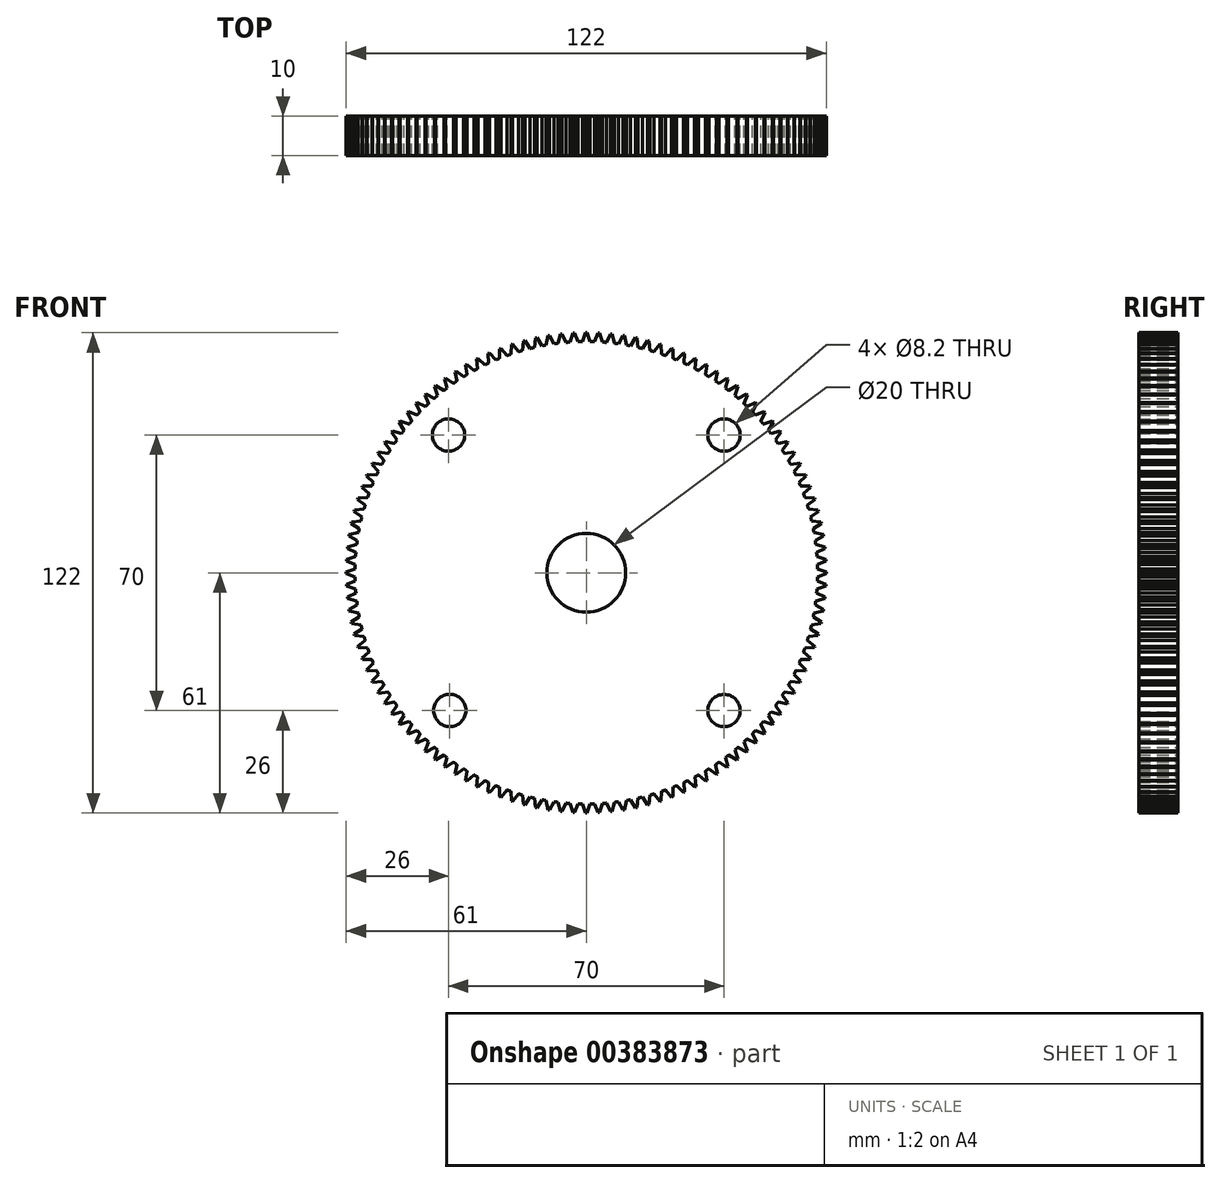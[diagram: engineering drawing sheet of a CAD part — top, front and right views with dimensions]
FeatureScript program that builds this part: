
annotation { "Feature Type Name" : "Feature", "Feature Type Description" : "" }
export const myFeature = defineFeature(function(context is Context, id is Id, definition is map)
    precondition{}
    {
        {
            var Q0;
            Q0=qCreatedBy(makeId("Front.planeOp"),FACE);
            var sketch = newSketch(context, id + "F0", { "sketchPlane" : qUnion([Q0])});
            skCircle(sketch, "E0", {"center": v(0, 0) * mm, "radius": 58.75 * mm});
            skCircle(sketch, "E1", {"center": v(0, 0) * mm, "radius": 61 * mm, "construction": true});
            skLineSegment(sketch, "E2", {"start": v(-1, 58.74) * mm, "end": v(-0.19, 61) * mm});
            skLineSegment(sketch, "E3", {"start": v(-0.19, 61) * mm, "end": v(0, 61) * mm});
            skLineSegment(sketch, "E4", {"start": v(-1, 58.74) * mm, "end": v(-1, 61.95) * mm, "construction": true});
            skLineSegment(sketch, "E5.MirrorCS", {"start": v(0.19, 61) * mm, "end": v(0, 61) * mm});
            skLineSegment(sketch, "E6.MirrorCS", {"start": v(1, 58.74) * mm, "end": v(0.19, 61) * mm});
            skLineSegment(sketch, "E7.1.0", {"start": v(-4.08, 58.6) * mm, "end": v(-3.38, 60.9) * mm});
            skLineSegment(sketch, "E7.1.1", {"start": v(-3.38, 60.9) * mm, "end": v(-3.2, 60.92) * mm});
            skLineSegment(sketch, "E7.1.2", {"start": v(-3, 60.93) * mm, "end": v(-3.2, 60.92) * mm});
            skLineSegment(sketch, "E7.1.3", {"start": v(-2.07, 58.71) * mm, "end": v(-3, 60.93) * mm});
            skLineSegment(sketch, "E7.2.0", {"start": v(-7.14, 58.31) * mm, "end": v(-6.56, 60.65) * mm});
            skLineSegment(sketch, "E7.2.1", {"start": v(-6.56, 60.65) * mm, "end": v(-6.38, 60.67) * mm});
            skLineSegment(sketch, "E7.2.2", {"start": v(-6.19, 60.69) * mm, "end": v(-6.38, 60.67) * mm});
            skLineSegment(sketch, "E7.2.3", {"start": v(-5.14, 58.53) * mm, "end": v(-6.19, 60.69) * mm});
            skLineSegment(sketch, "E7.3.0", {"start": v(-10.19, 57.86) * mm, "end": v(-9.73, 60.22) * mm});
            skLineSegment(sketch, "E7.3.1", {"start": v(-9.73, 60.22) * mm, "end": v(-9.54, 60.25) * mm});
            skLineSegment(sketch, "E7.3.2", {"start": v(-9.36, 60.28) * mm, "end": v(-9.54, 60.25) * mm});
            skLineSegment(sketch, "E7.3.3", {"start": v(-8.2, 58.18) * mm, "end": v(-9.36, 60.28) * mm});
            skLineSegment(sketch, "E7.4.0", {"start": v(-13.2, 57.25) * mm, "end": v(-12.87, 59.63) * mm});
            skLineSegment(sketch, "E7.4.1", {"start": v(-12.87, 59.63) * mm, "end": v(-12.68, 59.67) * mm});
            skLineSegment(sketch, "E7.4.2", {"start": v(-12.5, 59.7) * mm, "end": v(-12.68, 59.67) * mm});
            skLineSegment(sketch, "E7.4.3", {"start": v(-11.23, 57.67) * mm, "end": v(-12.5, 59.7) * mm});
            skLineSegment(sketch, "E7.5.0", {"start": v(-16.18, 56.48) * mm, "end": v(-15.97, 58.87) * mm});
            skLineSegment(sketch, "E7.5.1", {"start": v(-15.97, 58.87) * mm, "end": v(-15.79, 58.92) * mm});
            skLineSegment(sketch, "E7.5.2", {"start": v(-15.6, 58.97) * mm, "end": v(-15.79, 58.92) * mm});
            skLineSegment(sketch, "E7.5.3", {"start": v(-14.23, 57) * mm, "end": v(-15.6, 58.97) * mm});
            skLineSegment(sketch, "E7.6.0", {"start": v(-19.11, 55.55) * mm, "end": v(-19.03, 57.96) * mm});
            skLineSegment(sketch, "E7.6.1", {"start": v(-19.03, 57.96) * mm, "end": v(-18.85, 58.01) * mm});
            skLineSegment(sketch, "E7.6.2", {"start": v(-18.67, 58.07) * mm, "end": v(-18.85, 58.01) * mm});
            skLineSegment(sketch, "E7.6.3", {"start": v(-17.2, 56.18) * mm, "end": v(-18.67, 58.07) * mm});
            skLineSegment(sketch, "E7.7.0", {"start": v(-22, 54.48) * mm, "end": v(-22.04, 56.88) * mm});
            skLineSegment(sketch, "E7.7.1", {"start": v(-22.04, 56.88) * mm, "end": v(-21.86, 56.95) * mm});
            skLineSegment(sketch, "E7.7.2", {"start": v(-21.69, 57.02) * mm, "end": v(-21.86, 56.95) * mm});
            skLineSegment(sketch, "E7.7.3", {"start": v(-20.1, 55.2) * mm, "end": v(-21.69, 57.02) * mm});
            skLineSegment(sketch, "E7.8.0", {"start": v(-24.81, 53.25) * mm, "end": v(-24.98, 55.65) * mm});
            skLineSegment(sketch, "E7.8.1", {"start": v(-24.98, 55.65) * mm, "end": v(-24.81, 55.73) * mm});
            skLineSegment(sketch, "E7.8.2", {"start": v(-24.64, 55.8) * mm, "end": v(-24.81, 55.73) * mm});
            skLineSegment(sketch, "E7.8.3", {"start": v(-22.97, 54.07) * mm, "end": v(-24.64, 55.8) * mm});
            skLineSegment(sketch, "E7.9.0", {"start": v(-27.57, 51.88) * mm, "end": v(-27.86, 54.27) * mm});
            skLineSegment(sketch, "E7.9.1", {"start": v(-27.86, 54.27) * mm, "end": v(-27.7, 54.35) * mm});
            skLineSegment(sketch, "E7.9.2", {"start": v(-27.53, 54.44) * mm, "end": v(-27.7, 54.35) * mm});
            skLineSegment(sketch, "E7.9.3", {"start": v(-25.77, 52.8) * mm, "end": v(-27.53, 54.44) * mm});
            skLineSegment(sketch, "E7.10.0", {"start": v(-30.24, 50.37) * mm, "end": v(-30.66, 52.73) * mm});
            skLineSegment(sketch, "E7.10.1", {"start": v(-30.66, 52.73) * mm, "end": v(-30.5, 52.83) * mm});
            skLineSegment(sketch, "E7.10.2", {"start": v(-30.34, 52.92) * mm, "end": v(-30.5, 52.83) * mm});
            skLineSegment(sketch, "E7.10.3", {"start": v(-28.5, 51.38) * mm, "end": v(-30.34, 52.92) * mm});
            skLineSegment(sketch, "E7.11.0", {"start": v(-32.84, 48.71) * mm, "end": v(-33.38, 51.06) * mm});
            skLineSegment(sketch, "E7.11.1", {"start": v(-33.38, 51.06) * mm, "end": v(-33.22, 51.16) * mm});
            skLineSegment(sketch, "E7.11.2", {"start": v(-33.07, 51.26) * mm, "end": v(-33.22, 51.16) * mm});
            skLineSegment(sketch, "E7.11.3", {"start": v(-31.15, 49.81) * mm, "end": v(-33.07, 51.26) * mm});
            skLineSegment(sketch, "E8.1.12.0", {"start": v(-35.34, 46.93) * mm, "end": v(-36, 49.24) * mm});
            skLineSegment(sketch, "E8.3.12.0", {"start": v(-36, 49.24) * mm, "end": v(-35.85, 49.35) * mm});
            skLineSegment(sketch, "E8.6.12.0", {"start": v(-35.7, 49.46) * mm, "end": v(-35.85, 49.35) * mm});
            skLineSegment(sketch, "E8.9.12.0", {"start": v(-33.71, 48.12) * mm, "end": v(-35.7, 49.46) * mm});
            skLineSegment(sketch, "E8.1.13.0", {"start": v(-37.75, 45.02) * mm, "end": v(-38.53, 47.29) * mm});
            skLineSegment(sketch, "E8.3.13.0", {"start": v(-38.53, 47.29) * mm, "end": v(-38.39, 47.4) * mm});
            skLineSegment(sketch, "E8.6.13.0", {"start": v(-38.24, 47.52) * mm, "end": v(-38.39, 47.4) * mm});
            skLineSegment(sketch, "E8.9.13.0", {"start": v(-36.18, 46.29) * mm, "end": v(-38.24, 47.52) * mm});
            skLineSegment(sketch, "E8.1.14.0", {"start": v(-40.06, 42.98) * mm, "end": v(-40.96, 45.2) * mm});
            skLineSegment(sketch, "E8.3.14.0", {"start": v(-40.96, 45.2) * mm, "end": v(-40.82, 45.33) * mm});
            skLineSegment(sketch, "E8.6.14.0", {"start": v(-40.68, 45.46) * mm, "end": v(-40.82, 45.33) * mm});
            skLineSegment(sketch, "E8.9.14.0", {"start": v(-38.56, 44.33) * mm, "end": v(-40.68, 45.46) * mm});
            skLineSegment(sketch, "E8.1.15.0", {"start": v(-42.25, 40.82) * mm, "end": v(-43.27, 43) * mm});
            skLineSegment(sketch, "E8.3.15.0", {"start": v(-43.27, 43) * mm, "end": v(-43.13, 43.13) * mm});
            skLineSegment(sketch, "E8.6.15.0", {"start": v(-43, 43.27) * mm, "end": v(-43.13, 43.13) * mm});
            skLineSegment(sketch, "E8.9.15.0", {"start": v(-40.82, 42.25) * mm, "end": v(-43, 43.27) * mm});
            skLineSegment(sketch, "E8.1.16.0", {"start": v(-44.33, 38.56) * mm, "end": v(-45.46, 40.68) * mm});
            skLineSegment(sketch, "E8.3.16.0", {"start": v(-45.46, 40.68) * mm, "end": v(-45.33, 40.82) * mm});
            skLineSegment(sketch, "E8.6.16.0", {"start": v(-45.2, 40.96) * mm, "end": v(-45.33, 40.82) * mm});
            skLineSegment(sketch, "E8.9.16.0", {"start": v(-42.98, 40.06) * mm, "end": v(-45.2, 40.96) * mm});
            skLineSegment(sketch, "E8.1.17.0", {"start": v(-46.29, 36.18) * mm, "end": v(-47.52, 38.24) * mm});
            skLineSegment(sketch, "E8.3.17.0", {"start": v(-47.52, 38.24) * mm, "end": v(-47.4, 38.39) * mm});
            skLineSegment(sketch, "E8.6.17.0", {"start": v(-47.29, 38.53) * mm, "end": v(-47.4, 38.39) * mm});
            skLineSegment(sketch, "E8.9.17.0", {"start": v(-45.02, 37.75) * mm, "end": v(-47.29, 38.53) * mm});
            skLineSegment(sketch, "E8.1.18.0", {"start": v(-48.12, 33.71) * mm, "end": v(-49.46, 35.7) * mm});
            skLineSegment(sketch, "E8.3.18.0", {"start": v(-49.46, 35.7) * mm, "end": v(-49.35, 35.85) * mm});
            skLineSegment(sketch, "E8.6.18.0", {"start": v(-49.24, 36) * mm, "end": v(-49.35, 35.85) * mm});
            skLineSegment(sketch, "E8.9.18.0", {"start": v(-46.93, 35.34) * mm, "end": v(-49.24, 36) * mm});
            skLineSegment(sketch, "E8.1.19.0", {"start": v(-49.81, 31.15) * mm, "end": v(-51.26, 33.07) * mm});
            skLineSegment(sketch, "E8.3.19.0", {"start": v(-51.26, 33.07) * mm, "end": v(-51.16, 33.22) * mm});
            skLineSegment(sketch, "E8.6.19.0", {"start": v(-51.06, 33.38) * mm, "end": v(-51.16, 33.22) * mm});
            skLineSegment(sketch, "E8.9.19.0", {"start": v(-48.71, 32.84) * mm, "end": v(-51.06, 33.38) * mm});
            skLineSegment(sketch, "E8.1.20.0", {"start": v(-51.38, 28.5) * mm, "end": v(-52.92, 30.34) * mm});
            skLineSegment(sketch, "E8.3.20.0", {"start": v(-52.92, 30.34) * mm, "end": v(-52.83, 30.5) * mm});
            skLineSegment(sketch, "E8.6.20.0", {"start": v(-52.73, 30.66) * mm, "end": v(-52.83, 30.5) * mm});
            skLineSegment(sketch, "E8.9.20.0", {"start": v(-50.37, 30.24) * mm, "end": v(-52.73, 30.66) * mm});
            skLineSegment(sketch, "E8.1.21.0", {"start": v(-52.8, 25.77) * mm, "end": v(-54.44, 27.53) * mm});
            skLineSegment(sketch, "E8.3.21.0", {"start": v(-54.44, 27.53) * mm, "end": v(-54.35, 27.7) * mm});
            skLineSegment(sketch, "E8.6.21.0", {"start": v(-54.27, 27.86) * mm, "end": v(-54.35, 27.7) * mm});
            skLineSegment(sketch, "E8.9.21.0", {"start": v(-51.88, 27.57) * mm, "end": v(-54.27, 27.86) * mm});
            skLineSegment(sketch, "E8.1.22.0", {"start": v(-54.07, 22.97) * mm, "end": v(-55.8, 24.64) * mm});
            skLineSegment(sketch, "E8.3.22.0", {"start": v(-55.8, 24.64) * mm, "end": v(-55.73, 24.81) * mm});
            skLineSegment(sketch, "E8.6.22.0", {"start": v(-55.65, 24.98) * mm, "end": v(-55.73, 24.81) * mm});
            skLineSegment(sketch, "E8.9.22.0", {"start": v(-53.25, 24.81) * mm, "end": v(-55.65, 24.98) * mm});
            skLineSegment(sketch, "E8.1.23.0", {"start": v(-55.2, 20.1) * mm, "end": v(-57.02, 21.69) * mm});
            skLineSegment(sketch, "E8.3.23.0", {"start": v(-57.02, 21.69) * mm, "end": v(-56.95, 21.86) * mm});
            skLineSegment(sketch, "E8.6.23.0", {"start": v(-56.88, 22.04) * mm, "end": v(-56.95, 21.86) * mm});
            skLineSegment(sketch, "E8.9.23.0", {"start": v(-54.48, 22) * mm, "end": v(-56.88, 22.04) * mm});
            skLineSegment(sketch, "E8.1.24.0", {"start": v(-56.18, 17.2) * mm, "end": v(-58.07, 18.67) * mm});
            skLineSegment(sketch, "E8.3.24.0", {"start": v(-58.07, 18.67) * mm, "end": v(-58.01, 18.85) * mm});
            skLineSegment(sketch, "E8.6.24.0", {"start": v(-57.96, 19.03) * mm, "end": v(-58.01, 18.85) * mm});
            skLineSegment(sketch, "E8.9.24.0", {"start": v(-55.55, 19.11) * mm, "end": v(-57.96, 19.03) * mm});
            skLineSegment(sketch, "E8.1.25.0", {"start": v(-57, 14.23) * mm, "end": v(-58.97, 15.6) * mm});
            skLineSegment(sketch, "E8.3.25.0", {"start": v(-58.97, 15.6) * mm, "end": v(-58.92, 15.79) * mm});
            skLineSegment(sketch, "E8.6.25.0", {"start": v(-58.87, 15.97) * mm, "end": v(-58.92, 15.79) * mm});
            skLineSegment(sketch, "E8.9.25.0", {"start": v(-56.48, 16.18) * mm, "end": v(-58.87, 15.97) * mm});
            skLineSegment(sketch, "E8.1.26.0", {"start": v(-57.67, 11.23) * mm, "end": v(-59.7, 12.5) * mm});
            skLineSegment(sketch, "E8.3.26.0", {"start": v(-59.7, 12.5) * mm, "end": v(-59.67, 12.68) * mm});
            skLineSegment(sketch, "E8.6.26.0", {"start": v(-59.63, 12.87) * mm, "end": v(-59.67, 12.68) * mm});
            skLineSegment(sketch, "E8.9.26.0", {"start": v(-57.25, 13.2) * mm, "end": v(-59.63, 12.87) * mm});
            skLineSegment(sketch, "E8.1.27.0", {"start": v(-58.18, 8.2) * mm, "end": v(-60.28, 9.36) * mm});
            skLineSegment(sketch, "E8.3.27.0", {"start": v(-60.28, 9.36) * mm, "end": v(-60.25, 9.54) * mm});
            skLineSegment(sketch, "E8.6.27.0", {"start": v(-60.22, 9.73) * mm, "end": v(-60.25, 9.54) * mm});
            skLineSegment(sketch, "E8.9.27.0", {"start": v(-57.86, 10.19) * mm, "end": v(-60.22, 9.73) * mm});
            skLineSegment(sketch, "E8.1.28.0", {"start": v(-58.53, 5.14) * mm, "end": v(-60.69, 6.19) * mm});
            skLineSegment(sketch, "E8.3.28.0", {"start": v(-60.69, 6.19) * mm, "end": v(-60.67, 6.38) * mm});
            skLineSegment(sketch, "E8.6.28.0", {"start": v(-60.65, 6.56) * mm, "end": v(-60.67, 6.38) * mm});
            skLineSegment(sketch, "E8.9.28.0", {"start": v(-58.31, 7.14) * mm, "end": v(-60.65, 6.56) * mm});
            skLineSegment(sketch, "E8.1.29.0", {"start": v(-58.71, 2.07) * mm, "end": v(-60.93, 3) * mm});
            skLineSegment(sketch, "E8.3.29.0", {"start": v(-60.93, 3) * mm, "end": v(-60.92, 3.2) * mm});
            skLineSegment(sketch, "E8.6.29.0", {"start": v(-60.9, 3.38) * mm, "end": v(-60.92, 3.2) * mm});
            skLineSegment(sketch, "E8.9.29.0", {"start": v(-58.6, 4.08) * mm, "end": v(-60.9, 3.38) * mm});
            skLineSegment(sketch, "E8.1.30.0", {"start": v(-58.74, -1) * mm, "end": v(-61, -0.19) * mm});
            skLineSegment(sketch, "E8.3.30.0", {"start": v(-61, -0.19) * mm, "end": v(-61, 0) * mm});
            skLineSegment(sketch, "E8.6.30.0", {"start": v(-61, 0.19) * mm, "end": v(-61, 0) * mm});
            skLineSegment(sketch, "E8.9.30.0", {"start": v(-58.74, 1) * mm, "end": v(-61, 0.19) * mm});
            skLineSegment(sketch, "E8.1.31.0", {"start": v(-58.6, -4.08) * mm, "end": v(-60.9, -3.38) * mm});
            skLineSegment(sketch, "E8.3.31.0", {"start": v(-60.9, -3.38) * mm, "end": v(-60.92, -3.2) * mm});
            skLineSegment(sketch, "E8.6.31.0", {"start": v(-60.93, -3) * mm, "end": v(-60.92, -3.2) * mm});
            skLineSegment(sketch, "E8.9.31.0", {"start": v(-58.71, -2.07) * mm, "end": v(-60.93, -3) * mm});
            skLineSegment(sketch, "E8.1.32.0", {"start": v(-58.31, -7.14) * mm, "end": v(-60.65, -6.56) * mm});
            skLineSegment(sketch, "E8.3.32.0", {"start": v(-60.65, -6.56) * mm, "end": v(-60.67, -6.38) * mm});
            skLineSegment(sketch, "E8.6.32.0", {"start": v(-60.69, -6.19) * mm, "end": v(-60.67, -6.38) * mm});
            skLineSegment(sketch, "E8.9.32.0", {"start": v(-58.53, -5.14) * mm, "end": v(-60.69, -6.19) * mm});
            skLineSegment(sketch, "E8.1.33.0", {"start": v(-57.86, -10.19) * mm, "end": v(-60.22, -9.73) * mm});
            skLineSegment(sketch, "E8.3.33.0", {"start": v(-60.22, -9.73) * mm, "end": v(-60.25, -9.54) * mm});
            skLineSegment(sketch, "E8.6.33.0", {"start": v(-60.28, -9.36) * mm, "end": v(-60.25, -9.54) * mm});
            skLineSegment(sketch, "E8.9.33.0", {"start": v(-58.18, -8.2) * mm, "end": v(-60.28, -9.36) * mm});
            skLineSegment(sketch, "E8.1.34.0", {"start": v(-57.25, -13.2) * mm, "end": v(-59.63, -12.87) * mm});
            skLineSegment(sketch, "E8.3.34.0", {"start": v(-59.63, -12.87) * mm, "end": v(-59.67, -12.68) * mm});
            skLineSegment(sketch, "E8.6.34.0", {"start": v(-59.7, -12.5) * mm, "end": v(-59.67, -12.68) * mm});
            skLineSegment(sketch, "E8.9.34.0", {"start": v(-57.67, -11.23) * mm, "end": v(-59.7, -12.5) * mm});
            skLineSegment(sketch, "E8.1.35.0", {"start": v(-56.48, -16.18) * mm, "end": v(-58.87, -15.97) * mm});
            skLineSegment(sketch, "E8.3.35.0", {"start": v(-58.87, -15.97) * mm, "end": v(-58.92, -15.79) * mm});
            skLineSegment(sketch, "E8.6.35.0", {"start": v(-58.97, -15.6) * mm, "end": v(-58.92, -15.79) * mm});
            skLineSegment(sketch, "E8.9.35.0", {"start": v(-57, -14.23) * mm, "end": v(-58.97, -15.6) * mm});
            skLineSegment(sketch, "E8.1.36.0", {"start": v(-55.55, -19.11) * mm, "end": v(-57.96, -19.03) * mm});
            skLineSegment(sketch, "E8.3.36.0", {"start": v(-57.96, -19.03) * mm, "end": v(-58.01, -18.85) * mm});
            skLineSegment(sketch, "E8.6.36.0", {"start": v(-58.07, -18.67) * mm, "end": v(-58.01, -18.85) * mm});
            skLineSegment(sketch, "E8.9.36.0", {"start": v(-56.18, -17.2) * mm, "end": v(-58.07, -18.67) * mm});
            skLineSegment(sketch, "E8.1.37.0", {"start": v(-54.48, -22) * mm, "end": v(-56.88, -22.04) * mm});
            skLineSegment(sketch, "E8.3.37.0", {"start": v(-56.88, -22.04) * mm, "end": v(-56.95, -21.86) * mm});
            skLineSegment(sketch, "E8.6.37.0", {"start": v(-57.02, -21.69) * mm, "end": v(-56.95, -21.86) * mm});
            skLineSegment(sketch, "E8.9.37.0", {"start": v(-55.2, -20.1) * mm, "end": v(-57.02, -21.69) * mm});
            skLineSegment(sketch, "E8.1.38.0", {"start": v(-53.25, -24.81) * mm, "end": v(-55.65, -24.98) * mm});
            skLineSegment(sketch, "E8.3.38.0", {"start": v(-55.65, -24.98) * mm, "end": v(-55.73, -24.81) * mm});
            skLineSegment(sketch, "E8.6.38.0", {"start": v(-55.8, -24.64) * mm, "end": v(-55.73, -24.81) * mm});
            skLineSegment(sketch, "E8.9.38.0", {"start": v(-54.07, -22.97) * mm, "end": v(-55.8, -24.64) * mm});
            skLineSegment(sketch, "E8.1.39.0", {"start": v(-51.88, -27.57) * mm, "end": v(-54.27, -27.86) * mm});
            skLineSegment(sketch, "E8.3.39.0", {"start": v(-54.27, -27.86) * mm, "end": v(-54.35, -27.7) * mm});
            skLineSegment(sketch, "E8.6.39.0", {"start": v(-54.44, -27.53) * mm, "end": v(-54.35, -27.7) * mm});
            skLineSegment(sketch, "E8.9.39.0", {"start": v(-52.8, -25.77) * mm, "end": v(-54.44, -27.53) * mm});
            skLineSegment(sketch, "E8.1.40.0", {"start": v(-50.37, -30.24) * mm, "end": v(-52.73, -30.66) * mm});
            skLineSegment(sketch, "E8.3.40.0", {"start": v(-52.73, -30.66) * mm, "end": v(-52.83, -30.5) * mm});
            skLineSegment(sketch, "E8.6.40.0", {"start": v(-52.92, -30.34) * mm, "end": v(-52.83, -30.5) * mm});
            skLineSegment(sketch, "E8.9.40.0", {"start": v(-51.38, -28.5) * mm, "end": v(-52.92, -30.34) * mm});
            skLineSegment(sketch, "E8.1.41.0", {"start": v(-48.71, -32.84) * mm, "end": v(-51.06, -33.38) * mm});
            skLineSegment(sketch, "E8.3.41.0", {"start": v(-51.06, -33.38) * mm, "end": v(-51.16, -33.22) * mm});
            skLineSegment(sketch, "E8.6.41.0", {"start": v(-51.26, -33.07) * mm, "end": v(-51.16, -33.22) * mm});
            skLineSegment(sketch, "E8.9.41.0", {"start": v(-49.81, -31.15) * mm, "end": v(-51.26, -33.07) * mm});
            skLineSegment(sketch, "E8.1.42.0", {"start": v(-46.93, -35.34) * mm, "end": v(-49.24, -36) * mm});
            skLineSegment(sketch, "E8.3.42.0", {"start": v(-49.24, -36) * mm, "end": v(-49.35, -35.85) * mm});
            skLineSegment(sketch, "E8.6.42.0", {"start": v(-49.46, -35.7) * mm, "end": v(-49.35, -35.85) * mm});
            skLineSegment(sketch, "E8.9.42.0", {"start": v(-48.12, -33.71) * mm, "end": v(-49.46, -35.7) * mm});
            skLineSegment(sketch, "E8.1.43.0", {"start": v(-45.02, -37.75) * mm, "end": v(-47.29, -38.53) * mm});
            skLineSegment(sketch, "E8.3.43.0", {"start": v(-47.29, -38.53) * mm, "end": v(-47.4, -38.39) * mm});
            skLineSegment(sketch, "E8.6.43.0", {"start": v(-47.52, -38.24) * mm, "end": v(-47.4, -38.39) * mm});
            skLineSegment(sketch, "E8.9.43.0", {"start": v(-46.29, -36.18) * mm, "end": v(-47.52, -38.24) * mm});
            skLineSegment(sketch, "E8.1.44.0", {"start": v(-42.98, -40.06) * mm, "end": v(-45.2, -40.96) * mm});
            skLineSegment(sketch, "E8.3.44.0", {"start": v(-45.2, -40.96) * mm, "end": v(-45.33, -40.82) * mm});
            skLineSegment(sketch, "E8.6.44.0", {"start": v(-45.46, -40.68) * mm, "end": v(-45.33, -40.82) * mm});
            skLineSegment(sketch, "E8.9.44.0", {"start": v(-44.33, -38.56) * mm, "end": v(-45.46, -40.68) * mm});
            skLineSegment(sketch, "E8.1.45.0", {"start": v(-40.82, -42.25) * mm, "end": v(-43, -43.27) * mm});
            skLineSegment(sketch, "E8.3.45.0", {"start": v(-43, -43.27) * mm, "end": v(-43.13, -43.13) * mm});
            skLineSegment(sketch, "E8.6.45.0", {"start": v(-43.27, -43) * mm, "end": v(-43.13, -43.13) * mm});
            skLineSegment(sketch, "E8.9.45.0", {"start": v(-42.25, -40.82) * mm, "end": v(-43.27, -43) * mm});
            skLineSegment(sketch, "E8.1.46.0", {"start": v(-38.56, -44.33) * mm, "end": v(-40.68, -45.46) * mm});
            skLineSegment(sketch, "E8.3.46.0", {"start": v(-40.68, -45.46) * mm, "end": v(-40.82, -45.33) * mm});
            skLineSegment(sketch, "E8.6.46.0", {"start": v(-40.96, -45.2) * mm, "end": v(-40.82, -45.33) * mm});
            skLineSegment(sketch, "E8.9.46.0", {"start": v(-40.06, -42.98) * mm, "end": v(-40.96, -45.2) * mm});
            skLineSegment(sketch, "E8.1.47.0", {"start": v(-36.18, -46.29) * mm, "end": v(-38.24, -47.52) * mm});
            skLineSegment(sketch, "E8.3.47.0", {"start": v(-38.24, -47.52) * mm, "end": v(-38.39, -47.4) * mm});
            skLineSegment(sketch, "E8.6.47.0", {"start": v(-38.53, -47.29) * mm, "end": v(-38.39, -47.4) * mm});
            skLineSegment(sketch, "E8.9.47.0", {"start": v(-37.75, -45.02) * mm, "end": v(-38.53, -47.29) * mm});
            skLineSegment(sketch, "E8.1.48.0", {"start": v(-33.71, -48.12) * mm, "end": v(-35.7, -49.46) * mm});
            skLineSegment(sketch, "E8.3.48.0", {"start": v(-35.7, -49.46) * mm, "end": v(-35.85, -49.35) * mm});
            skLineSegment(sketch, "E8.6.48.0", {"start": v(-36, -49.24) * mm, "end": v(-35.85, -49.35) * mm});
            skLineSegment(sketch, "E8.9.48.0", {"start": v(-35.34, -46.93) * mm, "end": v(-36, -49.24) * mm});
            skLineSegment(sketch, "E8.1.49.0", {"start": v(-31.15, -49.81) * mm, "end": v(-33.07, -51.26) * mm});
            skLineSegment(sketch, "E8.3.49.0", {"start": v(-33.07, -51.26) * mm, "end": v(-33.22, -51.16) * mm});
            skLineSegment(sketch, "E8.6.49.0", {"start": v(-33.38, -51.06) * mm, "end": v(-33.22, -51.16) * mm});
            skLineSegment(sketch, "E8.9.49.0", {"start": v(-32.84, -48.71) * mm, "end": v(-33.38, -51.06) * mm});
            skLineSegment(sketch, "E8.1.50.0", {"start": v(-28.5, -51.38) * mm, "end": v(-30.34, -52.92) * mm});
            skLineSegment(sketch, "E8.3.50.0", {"start": v(-30.34, -52.92) * mm, "end": v(-30.5, -52.83) * mm});
            skLineSegment(sketch, "E8.6.50.0", {"start": v(-30.66, -52.73) * mm, "end": v(-30.5, -52.83) * mm});
            skLineSegment(sketch, "E8.9.50.0", {"start": v(-30.24, -50.37) * mm, "end": v(-30.66, -52.73) * mm});
            skLineSegment(sketch, "E8.1.51.0", {"start": v(-25.77, -52.8) * mm, "end": v(-27.53, -54.44) * mm});
            skLineSegment(sketch, "E8.3.51.0", {"start": v(-27.53, -54.44) * mm, "end": v(-27.7, -54.35) * mm});
            skLineSegment(sketch, "E8.6.51.0", {"start": v(-27.86, -54.27) * mm, "end": v(-27.7, -54.35) * mm});
            skLineSegment(sketch, "E8.9.51.0", {"start": v(-27.57, -51.88) * mm, "end": v(-27.86, -54.27) * mm});
            skLineSegment(sketch, "E8.1.52.0", {"start": v(-22.97, -54.07) * mm, "end": v(-24.64, -55.8) * mm});
            skLineSegment(sketch, "E8.3.52.0", {"start": v(-24.64, -55.8) * mm, "end": v(-24.81, -55.73) * mm});
            skLineSegment(sketch, "E8.6.52.0", {"start": v(-24.98, -55.65) * mm, "end": v(-24.81, -55.73) * mm});
            skLineSegment(sketch, "E8.9.52.0", {"start": v(-24.81, -53.25) * mm, "end": v(-24.98, -55.65) * mm});
            skLineSegment(sketch, "E8.1.53.0", {"start": v(-20.1, -55.2) * mm, "end": v(-21.69, -57.02) * mm});
            skLineSegment(sketch, "E8.3.53.0", {"start": v(-21.69, -57.02) * mm, "end": v(-21.86, -56.95) * mm});
            skLineSegment(sketch, "E8.6.53.0", {"start": v(-22.04, -56.88) * mm, "end": v(-21.86, -56.95) * mm});
            skLineSegment(sketch, "E8.9.53.0", {"start": v(-22, -54.48) * mm, "end": v(-22.04, -56.88) * mm});
            skLineSegment(sketch, "E8.1.54.0", {"start": v(-17.2, -56.18) * mm, "end": v(-18.67, -58.07) * mm});
            skLineSegment(sketch, "E8.3.54.0", {"start": v(-18.67, -58.07) * mm, "end": v(-18.85, -58.01) * mm});
            skLineSegment(sketch, "E8.6.54.0", {"start": v(-19.03, -57.96) * mm, "end": v(-18.85, -58.01) * mm});
            skLineSegment(sketch, "E8.9.54.0", {"start": v(-19.11, -55.55) * mm, "end": v(-19.03, -57.96) * mm});
            skLineSegment(sketch, "E8.1.55.0", {"start": v(-14.23, -57) * mm, "end": v(-15.6, -58.97) * mm});
            skLineSegment(sketch, "E8.3.55.0", {"start": v(-15.6, -58.97) * mm, "end": v(-15.79, -58.92) * mm});
            skLineSegment(sketch, "E8.6.55.0", {"start": v(-15.97, -58.87) * mm, "end": v(-15.79, -58.92) * mm});
            skLineSegment(sketch, "E8.9.55.0", {"start": v(-16.18, -56.48) * mm, "end": v(-15.97, -58.87) * mm});
            skLineSegment(sketch, "E8.1.56.0", {"start": v(-11.23, -57.67) * mm, "end": v(-12.5, -59.7) * mm});
            skLineSegment(sketch, "E8.3.56.0", {"start": v(-12.5, -59.7) * mm, "end": v(-12.68, -59.67) * mm});
            skLineSegment(sketch, "E8.6.56.0", {"start": v(-12.87, -59.63) * mm, "end": v(-12.68, -59.67) * mm});
            skLineSegment(sketch, "E8.9.56.0", {"start": v(-13.2, -57.25) * mm, "end": v(-12.87, -59.63) * mm});
            skLineSegment(sketch, "E8.1.57.0", {"start": v(-8.2, -58.18) * mm, "end": v(-9.36, -60.28) * mm});
            skLineSegment(sketch, "E8.3.57.0", {"start": v(-9.36, -60.28) * mm, "end": v(-9.54, -60.25) * mm});
            skLineSegment(sketch, "E8.6.57.0", {"start": v(-9.73, -60.22) * mm, "end": v(-9.54, -60.25) * mm});
            skLineSegment(sketch, "E8.9.57.0", {"start": v(-10.19, -57.86) * mm, "end": v(-9.73, -60.22) * mm});
            skLineSegment(sketch, "E8.1.58.0", {"start": v(-5.14, -58.53) * mm, "end": v(-6.19, -60.69) * mm});
            skLineSegment(sketch, "E8.3.58.0", {"start": v(-6.19, -60.69) * mm, "end": v(-6.38, -60.67) * mm});
            skLineSegment(sketch, "E8.6.58.0", {"start": v(-6.56, -60.65) * mm, "end": v(-6.38, -60.67) * mm});
            skLineSegment(sketch, "E8.9.58.0", {"start": v(-7.14, -58.31) * mm, "end": v(-6.56, -60.65) * mm});
            skLineSegment(sketch, "E8.1.59.0", {"start": v(-2.07, -58.71) * mm, "end": v(-3, -60.93) * mm});
            skLineSegment(sketch, "E8.3.59.0", {"start": v(-3, -60.93) * mm, "end": v(-3.2, -60.92) * mm});
            skLineSegment(sketch, "E8.6.59.0", {"start": v(-3.38, -60.9) * mm, "end": v(-3.2, -60.92) * mm});
            skLineSegment(sketch, "E8.9.59.0", {"start": v(-4.08, -58.6) * mm, "end": v(-3.38, -60.9) * mm});
            skLineSegment(sketch, "E8.1.60.0", {"start": v(1, -58.74) * mm, "end": v(0.19, -61) * mm});
            skLineSegment(sketch, "E8.3.60.0", {"start": v(0.19, -61) * mm, "end": v(0, -61) * mm});
            skLineSegment(sketch, "E8.6.60.0", {"start": v(-0.19, -61) * mm, "end": v(0, -61) * mm});
            skLineSegment(sketch, "E8.9.60.0", {"start": v(-1, -58.74) * mm, "end": v(-0.19, -61) * mm});
            skLineSegment(sketch, "E8.1.61.0", {"start": v(4.08, -58.6) * mm, "end": v(3.38, -60.9) * mm});
            skLineSegment(sketch, "E8.3.61.0", {"start": v(3.38, -60.9) * mm, "end": v(3.2, -60.92) * mm});
            skLineSegment(sketch, "E8.6.61.0", {"start": v(3, -60.93) * mm, "end": v(3.2, -60.92) * mm});
            skLineSegment(sketch, "E8.9.61.0", {"start": v(2.07, -58.71) * mm, "end": v(3, -60.93) * mm});
            skLineSegment(sketch, "E8.1.62.0", {"start": v(7.14, -58.31) * mm, "end": v(6.56, -60.65) * mm});
            skLineSegment(sketch, "E8.3.62.0", {"start": v(6.56, -60.65) * mm, "end": v(6.38, -60.67) * mm});
            skLineSegment(sketch, "E8.6.62.0", {"start": v(6.19, -60.69) * mm, "end": v(6.38, -60.67) * mm});
            skLineSegment(sketch, "E8.9.62.0", {"start": v(5.14, -58.53) * mm, "end": v(6.19, -60.69) * mm});
            skLineSegment(sketch, "E8.1.63.0", {"start": v(10.19, -57.86) * mm, "end": v(9.73, -60.22) * mm});
            skLineSegment(sketch, "E8.3.63.0", {"start": v(9.73, -60.22) * mm, "end": v(9.54, -60.25) * mm});
            skLineSegment(sketch, "E8.6.63.0", {"start": v(9.36, -60.28) * mm, "end": v(9.54, -60.25) * mm});
            skLineSegment(sketch, "E8.9.63.0", {"start": v(8.2, -58.18) * mm, "end": v(9.36, -60.28) * mm});
            skLineSegment(sketch, "E8.1.64.0", {"start": v(13.2, -57.25) * mm, "end": v(12.87, -59.63) * mm});
            skLineSegment(sketch, "E8.3.64.0", {"start": v(12.87, -59.63) * mm, "end": v(12.68, -59.67) * mm});
            skLineSegment(sketch, "E8.6.64.0", {"start": v(12.5, -59.7) * mm, "end": v(12.68, -59.67) * mm});
            skLineSegment(sketch, "E8.9.64.0", {"start": v(11.23, -57.67) * mm, "end": v(12.5, -59.7) * mm});
            skLineSegment(sketch, "E8.1.65.0", {"start": v(16.18, -56.48) * mm, "end": v(15.97, -58.87) * mm});
            skLineSegment(sketch, "E8.3.65.0", {"start": v(15.97, -58.87) * mm, "end": v(15.79, -58.92) * mm});
            skLineSegment(sketch, "E8.6.65.0", {"start": v(15.6, -58.97) * mm, "end": v(15.79, -58.92) * mm});
            skLineSegment(sketch, "E8.9.65.0", {"start": v(14.23, -57) * mm, "end": v(15.6, -58.97) * mm});
            skLineSegment(sketch, "E8.1.66.0", {"start": v(19.11, -55.55) * mm, "end": v(19.03, -57.96) * mm});
            skLineSegment(sketch, "E8.3.66.0", {"start": v(19.03, -57.96) * mm, "end": v(18.85, -58.01) * mm});
            skLineSegment(sketch, "E8.6.66.0", {"start": v(18.67, -58.07) * mm, "end": v(18.85, -58.01) * mm});
            skLineSegment(sketch, "E8.9.66.0", {"start": v(17.2, -56.18) * mm, "end": v(18.67, -58.07) * mm});
            skLineSegment(sketch, "E8.1.67.0", {"start": v(22, -54.48) * mm, "end": v(22.04, -56.88) * mm});
            skLineSegment(sketch, "E8.3.67.0", {"start": v(22.04, -56.88) * mm, "end": v(21.86, -56.95) * mm});
            skLineSegment(sketch, "E8.6.67.0", {"start": v(21.69, -57.02) * mm, "end": v(21.86, -56.95) * mm});
            skLineSegment(sketch, "E8.9.67.0", {"start": v(20.1, -55.2) * mm, "end": v(21.69, -57.02) * mm});
            skLineSegment(sketch, "E8.1.68.0", {"start": v(24.81, -53.25) * mm, "end": v(24.98, -55.65) * mm});
            skLineSegment(sketch, "E8.3.68.0", {"start": v(24.98, -55.65) * mm, "end": v(24.81, -55.73) * mm});
            skLineSegment(sketch, "E8.6.68.0", {"start": v(24.64, -55.8) * mm, "end": v(24.81, -55.73) * mm});
            skLineSegment(sketch, "E8.9.68.0", {"start": v(22.97, -54.07) * mm, "end": v(24.64, -55.8) * mm});
            skLineSegment(sketch, "E8.1.69.0", {"start": v(27.57, -51.88) * mm, "end": v(27.86, -54.27) * mm});
            skLineSegment(sketch, "E8.3.69.0", {"start": v(27.86, -54.27) * mm, "end": v(27.7, -54.35) * mm});
            skLineSegment(sketch, "E8.6.69.0", {"start": v(27.53, -54.44) * mm, "end": v(27.7, -54.35) * mm});
            skLineSegment(sketch, "E8.9.69.0", {"start": v(25.77, -52.8) * mm, "end": v(27.53, -54.44) * mm});
            skLineSegment(sketch, "E8.1.70.0", {"start": v(30.24, -50.37) * mm, "end": v(30.66, -52.73) * mm});
            skLineSegment(sketch, "E8.3.70.0", {"start": v(30.66, -52.73) * mm, "end": v(30.5, -52.83) * mm});
            skLineSegment(sketch, "E8.6.70.0", {"start": v(30.34, -52.92) * mm, "end": v(30.5, -52.83) * mm});
            skLineSegment(sketch, "E8.9.70.0", {"start": v(28.5, -51.38) * mm, "end": v(30.34, -52.92) * mm});
            skLineSegment(sketch, "E8.1.71.0", {"start": v(32.84, -48.71) * mm, "end": v(33.38, -51.06) * mm});
            skLineSegment(sketch, "E8.3.71.0", {"start": v(33.38, -51.06) * mm, "end": v(33.22, -51.16) * mm});
            skLineSegment(sketch, "E8.6.71.0", {"start": v(33.07, -51.26) * mm, "end": v(33.22, -51.16) * mm});
            skLineSegment(sketch, "E8.9.71.0", {"start": v(31.15, -49.81) * mm, "end": v(33.07, -51.26) * mm});
            skLineSegment(sketch, "E8.1.72.0", {"start": v(35.34, -46.93) * mm, "end": v(36, -49.24) * mm});
            skLineSegment(sketch, "E8.3.72.0", {"start": v(36, -49.24) * mm, "end": v(35.85, -49.35) * mm});
            skLineSegment(sketch, "E8.6.72.0", {"start": v(35.7, -49.46) * mm, "end": v(35.85, -49.35) * mm});
            skLineSegment(sketch, "E8.9.72.0", {"start": v(33.71, -48.12) * mm, "end": v(35.7, -49.46) * mm});
            skLineSegment(sketch, "E8.1.73.0", {"start": v(37.75, -45.02) * mm, "end": v(38.53, -47.29) * mm});
            skLineSegment(sketch, "E8.3.73.0", {"start": v(38.53, -47.29) * mm, "end": v(38.39, -47.4) * mm});
            skLineSegment(sketch, "E8.6.73.0", {"start": v(38.24, -47.52) * mm, "end": v(38.39, -47.4) * mm});
            skLineSegment(sketch, "E8.9.73.0", {"start": v(36.18, -46.29) * mm, "end": v(38.24, -47.52) * mm});
            skLineSegment(sketch, "E8.1.74.0", {"start": v(40.06, -42.98) * mm, "end": v(40.96, -45.2) * mm});
            skLineSegment(sketch, "E8.3.74.0", {"start": v(40.96, -45.2) * mm, "end": v(40.82, -45.33) * mm});
            skLineSegment(sketch, "E8.6.74.0", {"start": v(40.68, -45.46) * mm, "end": v(40.82, -45.33) * mm});
            skLineSegment(sketch, "E8.9.74.0", {"start": v(38.56, -44.33) * mm, "end": v(40.68, -45.46) * mm});
            skLineSegment(sketch, "E8.1.75.0", {"start": v(42.25, -40.82) * mm, "end": v(43.27, -43) * mm});
            skLineSegment(sketch, "E8.3.75.0", {"start": v(43.27, -43) * mm, "end": v(43.13, -43.13) * mm});
            skLineSegment(sketch, "E8.6.75.0", {"start": v(43, -43.27) * mm, "end": v(43.13, -43.13) * mm});
            skLineSegment(sketch, "E8.9.75.0", {"start": v(40.82, -42.25) * mm, "end": v(43, -43.27) * mm});
            skLineSegment(sketch, "E8.1.76.0", {"start": v(44.33, -38.56) * mm, "end": v(45.46, -40.68) * mm});
            skLineSegment(sketch, "E8.3.76.0", {"start": v(45.46, -40.68) * mm, "end": v(45.33, -40.82) * mm});
            skLineSegment(sketch, "E8.6.76.0", {"start": v(45.2, -40.96) * mm, "end": v(45.33, -40.82) * mm});
            skLineSegment(sketch, "E8.9.76.0", {"start": v(42.98, -40.06) * mm, "end": v(45.2, -40.96) * mm});
            skLineSegment(sketch, "E8.1.77.0", {"start": v(46.29, -36.18) * mm, "end": v(47.52, -38.24) * mm});
            skLineSegment(sketch, "E8.3.77.0", {"start": v(47.52, -38.24) * mm, "end": v(47.4, -38.39) * mm});
            skLineSegment(sketch, "E8.6.77.0", {"start": v(47.29, -38.53) * mm, "end": v(47.4, -38.39) * mm});
            skLineSegment(sketch, "E8.9.77.0", {"start": v(45.02, -37.75) * mm, "end": v(47.29, -38.53) * mm});
            skLineSegment(sketch, "E8.1.78.0", {"start": v(48.12, -33.71) * mm, "end": v(49.46, -35.7) * mm});
            skLineSegment(sketch, "E8.3.78.0", {"start": v(49.46, -35.7) * mm, "end": v(49.35, -35.85) * mm});
            skLineSegment(sketch, "E8.6.78.0", {"start": v(49.24, -36) * mm, "end": v(49.35, -35.85) * mm});
            skLineSegment(sketch, "E8.9.78.0", {"start": v(46.93, -35.34) * mm, "end": v(49.24, -36) * mm});
            skLineSegment(sketch, "E8.1.79.0", {"start": v(49.81, -31.15) * mm, "end": v(51.26, -33.07) * mm});
            skLineSegment(sketch, "E8.3.79.0", {"start": v(51.26, -33.07) * mm, "end": v(51.16, -33.22) * mm});
            skLineSegment(sketch, "E8.6.79.0", {"start": v(51.06, -33.38) * mm, "end": v(51.16, -33.22) * mm});
            skLineSegment(sketch, "E8.9.79.0", {"start": v(48.71, -32.84) * mm, "end": v(51.06, -33.38) * mm});
            skLineSegment(sketch, "E8.1.80.0", {"start": v(51.38, -28.5) * mm, "end": v(52.92, -30.34) * mm});
            skLineSegment(sketch, "E8.3.80.0", {"start": v(52.92, -30.34) * mm, "end": v(52.83, -30.5) * mm});
            skLineSegment(sketch, "E8.6.80.0", {"start": v(52.73, -30.66) * mm, "end": v(52.83, -30.5) * mm});
            skLineSegment(sketch, "E8.9.80.0", {"start": v(50.37, -30.24) * mm, "end": v(52.73, -30.66) * mm});
            skLineSegment(sketch, "E8.1.81.0", {"start": v(52.8, -25.77) * mm, "end": v(54.44, -27.53) * mm});
            skLineSegment(sketch, "E8.3.81.0", {"start": v(54.44, -27.53) * mm, "end": v(54.35, -27.7) * mm});
            skLineSegment(sketch, "E8.6.81.0", {"start": v(54.27, -27.86) * mm, "end": v(54.35, -27.7) * mm});
            skLineSegment(sketch, "E8.9.81.0", {"start": v(51.88, -27.57) * mm, "end": v(54.27, -27.86) * mm});
            skLineSegment(sketch, "E8.1.82.0", {"start": v(54.07, -22.97) * mm, "end": v(55.8, -24.64) * mm});
            skLineSegment(sketch, "E8.3.82.0", {"start": v(55.8, -24.64) * mm, "end": v(55.73, -24.81) * mm});
            skLineSegment(sketch, "E8.6.82.0", {"start": v(55.65, -24.98) * mm, "end": v(55.73, -24.81) * mm});
            skLineSegment(sketch, "E8.9.82.0", {"start": v(53.25, -24.81) * mm, "end": v(55.65, -24.98) * mm});
            skLineSegment(sketch, "E8.1.83.0", {"start": v(55.2, -20.1) * mm, "end": v(57.02, -21.69) * mm});
            skLineSegment(sketch, "E8.3.83.0", {"start": v(57.02, -21.69) * mm, "end": v(56.95, -21.86) * mm});
            skLineSegment(sketch, "E8.6.83.0", {"start": v(56.88, -22.04) * mm, "end": v(56.95, -21.86) * mm});
            skLineSegment(sketch, "E8.9.83.0", {"start": v(54.48, -22) * mm, "end": v(56.88, -22.04) * mm});
            skLineSegment(sketch, "E8.1.84.0", {"start": v(56.18, -17.2) * mm, "end": v(58.07, -18.67) * mm});
            skLineSegment(sketch, "E8.3.84.0", {"start": v(58.07, -18.67) * mm, "end": v(58.01, -18.85) * mm});
            skLineSegment(sketch, "E8.6.84.0", {"start": v(57.96, -19.03) * mm, "end": v(58.01, -18.85) * mm});
            skLineSegment(sketch, "E8.9.84.0", {"start": v(55.55, -19.11) * mm, "end": v(57.96, -19.03) * mm});
            skLineSegment(sketch, "E8.1.85.0", {"start": v(57, -14.23) * mm, "end": v(58.97, -15.6) * mm});
            skLineSegment(sketch, "E8.3.85.0", {"start": v(58.97, -15.6) * mm, "end": v(58.92, -15.79) * mm});
            skLineSegment(sketch, "E8.6.85.0", {"start": v(58.87, -15.97) * mm, "end": v(58.92, -15.79) * mm});
            skLineSegment(sketch, "E8.9.85.0", {"start": v(56.48, -16.18) * mm, "end": v(58.87, -15.97) * mm});
            skLineSegment(sketch, "E8.1.86.0", {"start": v(57.67, -11.23) * mm, "end": v(59.7, -12.5) * mm});
            skLineSegment(sketch, "E8.3.86.0", {"start": v(59.7, -12.5) * mm, "end": v(59.67, -12.68) * mm});
            skLineSegment(sketch, "E8.6.86.0", {"start": v(59.63, -12.87) * mm, "end": v(59.67, -12.68) * mm});
            skLineSegment(sketch, "E8.9.86.0", {"start": v(57.25, -13.2) * mm, "end": v(59.63, -12.87) * mm});
            skLineSegment(sketch, "E8.1.87.0", {"start": v(58.18, -8.2) * mm, "end": v(60.28, -9.36) * mm});
            skLineSegment(sketch, "E8.3.87.0", {"start": v(60.28, -9.36) * mm, "end": v(60.25, -9.54) * mm});
            skLineSegment(sketch, "E8.6.87.0", {"start": v(60.22, -9.73) * mm, "end": v(60.25, -9.54) * mm});
            skLineSegment(sketch, "E8.9.87.0", {"start": v(57.86, -10.19) * mm, "end": v(60.22, -9.73) * mm});
            skLineSegment(sketch, "E8.1.88.0", {"start": v(58.53, -5.14) * mm, "end": v(60.69, -6.19) * mm});
            skLineSegment(sketch, "E8.3.88.0", {"start": v(60.69, -6.19) * mm, "end": v(60.67, -6.38) * mm});
            skLineSegment(sketch, "E8.6.88.0", {"start": v(60.65, -6.56) * mm, "end": v(60.67, -6.38) * mm});
            skLineSegment(sketch, "E8.9.88.0", {"start": v(58.31, -7.14) * mm, "end": v(60.65, -6.56) * mm});
            skLineSegment(sketch, "E8.1.89.0", {"start": v(58.71, -2.07) * mm, "end": v(60.93, -3) * mm});
            skLineSegment(sketch, "E8.3.89.0", {"start": v(60.93, -3) * mm, "end": v(60.92, -3.2) * mm});
            skLineSegment(sketch, "E8.6.89.0", {"start": v(60.9, -3.38) * mm, "end": v(60.92, -3.2) * mm});
            skLineSegment(sketch, "E8.9.89.0", {"start": v(58.6, -4.08) * mm, "end": v(60.9, -3.38) * mm});
            skLineSegment(sketch, "E8.1.90.0", {"start": v(58.74, 1) * mm, "end": v(61, 0.19) * mm});
            skLineSegment(sketch, "E8.3.90.0", {"start": v(61, 0.19) * mm, "end": v(61, 0) * mm});
            skLineSegment(sketch, "E8.6.90.0", {"start": v(61, -0.19) * mm, "end": v(61, 0) * mm});
            skLineSegment(sketch, "E8.9.90.0", {"start": v(58.74, -1) * mm, "end": v(61, -0.19) * mm});
            skLineSegment(sketch, "E8.1.91.0", {"start": v(58.6, 4.08) * mm, "end": v(60.9, 3.38) * mm});
            skLineSegment(sketch, "E8.3.91.0", {"start": v(60.9, 3.38) * mm, "end": v(60.92, 3.2) * mm});
            skLineSegment(sketch, "E8.6.91.0", {"start": v(60.93, 3) * mm, "end": v(60.92, 3.2) * mm});
            skLineSegment(sketch, "E8.9.91.0", {"start": v(58.71, 2.07) * mm, "end": v(60.93, 3) * mm});
            skLineSegment(sketch, "E8.1.92.0", {"start": v(58.31, 7.14) * mm, "end": v(60.65, 6.56) * mm});
            skLineSegment(sketch, "E8.3.92.0", {"start": v(60.65, 6.56) * mm, "end": v(60.67, 6.38) * mm});
            skLineSegment(sketch, "E8.6.92.0", {"start": v(60.69, 6.19) * mm, "end": v(60.67, 6.38) * mm});
            skLineSegment(sketch, "E8.9.92.0", {"start": v(58.53, 5.14) * mm, "end": v(60.69, 6.19) * mm});
            skLineSegment(sketch, "E8.1.93.0", {"start": v(57.86, 10.19) * mm, "end": v(60.22, 9.73) * mm});
            skLineSegment(sketch, "E8.3.93.0", {"start": v(60.22, 9.73) * mm, "end": v(60.25, 9.54) * mm});
            skLineSegment(sketch, "E8.6.93.0", {"start": v(60.28, 9.36) * mm, "end": v(60.25, 9.54) * mm});
            skLineSegment(sketch, "E8.9.93.0", {"start": v(58.18, 8.2) * mm, "end": v(60.28, 9.36) * mm});
            skLineSegment(sketch, "E8.1.94.0", {"start": v(57.25, 13.2) * mm, "end": v(59.63, 12.87) * mm});
            skLineSegment(sketch, "E8.3.94.0", {"start": v(59.63, 12.87) * mm, "end": v(59.67, 12.68) * mm});
            skLineSegment(sketch, "E8.6.94.0", {"start": v(59.7, 12.5) * mm, "end": v(59.67, 12.68) * mm});
            skLineSegment(sketch, "E8.9.94.0", {"start": v(57.67, 11.23) * mm, "end": v(59.7, 12.5) * mm});
            skLineSegment(sketch, "E8.1.95.0", {"start": v(56.48, 16.18) * mm, "end": v(58.87, 15.97) * mm});
            skLineSegment(sketch, "E8.3.95.0", {"start": v(58.87, 15.97) * mm, "end": v(58.92, 15.79) * mm});
            skLineSegment(sketch, "E8.6.95.0", {"start": v(58.97, 15.6) * mm, "end": v(58.92, 15.79) * mm});
            skLineSegment(sketch, "E8.9.95.0", {"start": v(57, 14.23) * mm, "end": v(58.97, 15.6) * mm});
            skLineSegment(sketch, "E8.1.96.0", {"start": v(55.55, 19.11) * mm, "end": v(57.96, 19.03) * mm});
            skLineSegment(sketch, "E8.3.96.0", {"start": v(57.96, 19.03) * mm, "end": v(58.01, 18.85) * mm});
            skLineSegment(sketch, "E8.6.96.0", {"start": v(58.07, 18.67) * mm, "end": v(58.01, 18.85) * mm});
            skLineSegment(sketch, "E8.9.96.0", {"start": v(56.18, 17.2) * mm, "end": v(58.07, 18.67) * mm});
            skLineSegment(sketch, "E8.1.97.0", {"start": v(54.48, 22) * mm, "end": v(56.88, 22.04) * mm});
            skLineSegment(sketch, "E8.3.97.0", {"start": v(56.88, 22.04) * mm, "end": v(56.95, 21.86) * mm});
            skLineSegment(sketch, "E8.6.97.0", {"start": v(57.02, 21.69) * mm, "end": v(56.95, 21.86) * mm});
            skLineSegment(sketch, "E8.9.97.0", {"start": v(55.2, 20.1) * mm, "end": v(57.02, 21.69) * mm});
            skLineSegment(sketch, "E8.1.98.0", {"start": v(53.25, 24.81) * mm, "end": v(55.65, 24.98) * mm});
            skLineSegment(sketch, "E8.3.98.0", {"start": v(55.65, 24.98) * mm, "end": v(55.73, 24.81) * mm});
            skLineSegment(sketch, "E8.6.98.0", {"start": v(55.8, 24.64) * mm, "end": v(55.73, 24.81) * mm});
            skLineSegment(sketch, "E8.9.98.0", {"start": v(54.07, 22.97) * mm, "end": v(55.8, 24.64) * mm});
            skLineSegment(sketch, "E8.1.99.0", {"start": v(51.88, 27.57) * mm, "end": v(54.27, 27.86) * mm});
            skLineSegment(sketch, "E8.3.99.0", {"start": v(54.27, 27.86) * mm, "end": v(54.35, 27.7) * mm});
            skLineSegment(sketch, "E8.6.99.0", {"start": v(54.44, 27.53) * mm, "end": v(54.35, 27.7) * mm});
            skLineSegment(sketch, "E8.9.99.0", {"start": v(52.8, 25.77) * mm, "end": v(54.44, 27.53) * mm});
            skLineSegment(sketch, "E8.1.100.0", {"start": v(50.37, 30.24) * mm, "end": v(52.73, 30.66) * mm});
            skLineSegment(sketch, "E8.3.100.0", {"start": v(52.73, 30.66) * mm, "end": v(52.83, 30.5) * mm});
            skLineSegment(sketch, "E8.6.100.0", {"start": v(52.92, 30.34) * mm, "end": v(52.83, 30.5) * mm});
            skLineSegment(sketch, "E8.9.100.0", {"start": v(51.38, 28.5) * mm, "end": v(52.92, 30.34) * mm});
            skLineSegment(sketch, "E8.1.101.0", {"start": v(48.71, 32.84) * mm, "end": v(51.06, 33.38) * mm});
            skLineSegment(sketch, "E8.3.101.0", {"start": v(51.06, 33.38) * mm, "end": v(51.16, 33.22) * mm});
            skLineSegment(sketch, "E8.6.101.0", {"start": v(51.26, 33.07) * mm, "end": v(51.16, 33.22) * mm});
            skLineSegment(sketch, "E8.9.101.0", {"start": v(49.81, 31.15) * mm, "end": v(51.26, 33.07) * mm});
            skLineSegment(sketch, "E8.1.102.0", {"start": v(46.93, 35.34) * mm, "end": v(49.24, 36) * mm});
            skLineSegment(sketch, "E8.3.102.0", {"start": v(49.24, 36) * mm, "end": v(49.35, 35.85) * mm});
            skLineSegment(sketch, "E8.6.102.0", {"start": v(49.46, 35.7) * mm, "end": v(49.35, 35.85) * mm});
            skLineSegment(sketch, "E8.9.102.0", {"start": v(48.12, 33.71) * mm, "end": v(49.46, 35.7) * mm});
            skLineSegment(sketch, "E8.1.103.0", {"start": v(45.02, 37.75) * mm, "end": v(47.29, 38.53) * mm});
            skLineSegment(sketch, "E8.3.103.0", {"start": v(47.29, 38.53) * mm, "end": v(47.4, 38.39) * mm});
            skLineSegment(sketch, "E8.6.103.0", {"start": v(47.52, 38.24) * mm, "end": v(47.4, 38.39) * mm});
            skLineSegment(sketch, "E8.9.103.0", {"start": v(46.29, 36.18) * mm, "end": v(47.52, 38.24) * mm});
            skLineSegment(sketch, "E8.1.104.0", {"start": v(42.98, 40.06) * mm, "end": v(45.2, 40.96) * mm});
            skLineSegment(sketch, "E8.3.104.0", {"start": v(45.2, 40.96) * mm, "end": v(45.33, 40.82) * mm});
            skLineSegment(sketch, "E8.6.104.0", {"start": v(45.46, 40.68) * mm, "end": v(45.33, 40.82) * mm});
            skLineSegment(sketch, "E8.9.104.0", {"start": v(44.33, 38.56) * mm, "end": v(45.46, 40.68) * mm});
            skLineSegment(sketch, "E8.1.105.0", {"start": v(40.82, 42.25) * mm, "end": v(43, 43.27) * mm});
            skLineSegment(sketch, "E8.3.105.0", {"start": v(43, 43.27) * mm, "end": v(43.13, 43.13) * mm});
            skLineSegment(sketch, "E8.6.105.0", {"start": v(43.27, 43) * mm, "end": v(43.13, 43.13) * mm});
            skLineSegment(sketch, "E8.9.105.0", {"start": v(42.25, 40.82) * mm, "end": v(43.27, 43) * mm});
            skLineSegment(sketch, "E8.1.106.0", {"start": v(38.56, 44.33) * mm, "end": v(40.68, 45.46) * mm});
            skLineSegment(sketch, "E8.3.106.0", {"start": v(40.68, 45.46) * mm, "end": v(40.82, 45.33) * mm});
            skLineSegment(sketch, "E8.6.106.0", {"start": v(40.96, 45.2) * mm, "end": v(40.82, 45.33) * mm});
            skLineSegment(sketch, "E8.9.106.0", {"start": v(40.06, 42.98) * mm, "end": v(40.96, 45.2) * mm});
            skLineSegment(sketch, "E8.1.107.0", {"start": v(36.18, 46.29) * mm, "end": v(38.24, 47.52) * mm});
            skLineSegment(sketch, "E8.3.107.0", {"start": v(38.24, 47.52) * mm, "end": v(38.39, 47.4) * mm});
            skLineSegment(sketch, "E8.6.107.0", {"start": v(38.53, 47.29) * mm, "end": v(38.39, 47.4) * mm});
            skLineSegment(sketch, "E8.9.107.0", {"start": v(37.75, 45.02) * mm, "end": v(38.53, 47.29) * mm});
            skLineSegment(sketch, "E8.1.108.0", {"start": v(33.71, 48.12) * mm, "end": v(35.7, 49.46) * mm});
            skLineSegment(sketch, "E8.3.108.0", {"start": v(35.7, 49.46) * mm, "end": v(35.85, 49.35) * mm});
            skLineSegment(sketch, "E8.6.108.0", {"start": v(36, 49.24) * mm, "end": v(35.85, 49.35) * mm});
            skLineSegment(sketch, "E8.9.108.0", {"start": v(35.34, 46.93) * mm, "end": v(36, 49.24) * mm});
            skLineSegment(sketch, "E8.1.109.0", {"start": v(31.15, 49.81) * mm, "end": v(33.07, 51.26) * mm});
            skLineSegment(sketch, "E8.3.109.0", {"start": v(33.07, 51.26) * mm, "end": v(33.22, 51.16) * mm});
            skLineSegment(sketch, "E8.6.109.0", {"start": v(33.38, 51.06) * mm, "end": v(33.22, 51.16) * mm});
            skLineSegment(sketch, "E8.9.109.0", {"start": v(32.84, 48.71) * mm, "end": v(33.38, 51.06) * mm});
            skLineSegment(sketch, "E8.1.110.0", {"start": v(28.5, 51.38) * mm, "end": v(30.34, 52.92) * mm});
            skLineSegment(sketch, "E8.3.110.0", {"start": v(30.34, 52.92) * mm, "end": v(30.5, 52.83) * mm});
            skLineSegment(sketch, "E8.6.110.0", {"start": v(30.66, 52.73) * mm, "end": v(30.5, 52.83) * mm});
            skLineSegment(sketch, "E8.9.110.0", {"start": v(30.24, 50.37) * mm, "end": v(30.66, 52.73) * mm});
            skLineSegment(sketch, "E8.1.111.0", {"start": v(25.77, 52.8) * mm, "end": v(27.53, 54.44) * mm});
            skLineSegment(sketch, "E8.3.111.0", {"start": v(27.53, 54.44) * mm, "end": v(27.7, 54.35) * mm});
            skLineSegment(sketch, "E8.6.111.0", {"start": v(27.86, 54.27) * mm, "end": v(27.7, 54.35) * mm});
            skLineSegment(sketch, "E8.9.111.0", {"start": v(27.57, 51.88) * mm, "end": v(27.86, 54.27) * mm});
            skLineSegment(sketch, "E8.1.112.0", {"start": v(22.97, 54.07) * mm, "end": v(24.64, 55.8) * mm});
            skLineSegment(sketch, "E8.3.112.0", {"start": v(24.64, 55.8) * mm, "end": v(24.81, 55.73) * mm});
            skLineSegment(sketch, "E8.6.112.0", {"start": v(24.98, 55.65) * mm, "end": v(24.81, 55.73) * mm});
            skLineSegment(sketch, "E8.9.112.0", {"start": v(24.81, 53.25) * mm, "end": v(24.98, 55.65) * mm});
            skLineSegment(sketch, "E8.1.113.0", {"start": v(20.1, 55.2) * mm, "end": v(21.69, 57.02) * mm});
            skLineSegment(sketch, "E8.3.113.0", {"start": v(21.69, 57.02) * mm, "end": v(21.86, 56.95) * mm});
            skLineSegment(sketch, "E8.6.113.0", {"start": v(22.04, 56.88) * mm, "end": v(21.86, 56.95) * mm});
            skLineSegment(sketch, "E8.9.113.0", {"start": v(22, 54.48) * mm, "end": v(22.04, 56.88) * mm});
            skLineSegment(sketch, "E8.1.114.0", {"start": v(17.2, 56.18) * mm, "end": v(18.67, 58.07) * mm});
            skLineSegment(sketch, "E8.3.114.0", {"start": v(18.67, 58.07) * mm, "end": v(18.85, 58.01) * mm});
            skLineSegment(sketch, "E8.6.114.0", {"start": v(19.03, 57.96) * mm, "end": v(18.85, 58.01) * mm});
            skLineSegment(sketch, "E8.9.114.0", {"start": v(19.11, 55.55) * mm, "end": v(19.03, 57.96) * mm});
            skLineSegment(sketch, "E8.1.115.0", {"start": v(14.23, 57) * mm, "end": v(15.6, 58.97) * mm});
            skLineSegment(sketch, "E8.3.115.0", {"start": v(15.6, 58.97) * mm, "end": v(15.79, 58.92) * mm});
            skLineSegment(sketch, "E8.6.115.0", {"start": v(15.97, 58.87) * mm, "end": v(15.79, 58.92) * mm});
            skLineSegment(sketch, "E8.9.115.0", {"start": v(16.18, 56.48) * mm, "end": v(15.97, 58.87) * mm});
            skLineSegment(sketch, "E8.1.116.0", {"start": v(11.23, 57.67) * mm, "end": v(12.5, 59.7) * mm});
            skLineSegment(sketch, "E8.3.116.0", {"start": v(12.5, 59.7) * mm, "end": v(12.68, 59.67) * mm});
            skLineSegment(sketch, "E8.6.116.0", {"start": v(12.87, 59.63) * mm, "end": v(12.68, 59.67) * mm});
            skLineSegment(sketch, "E8.9.116.0", {"start": v(13.2, 57.25) * mm, "end": v(12.87, 59.63) * mm});
            skLineSegment(sketch, "E8.1.117.0", {"start": v(8.2, 58.18) * mm, "end": v(9.36, 60.28) * mm});
            skLineSegment(sketch, "E8.3.117.0", {"start": v(9.36, 60.28) * mm, "end": v(9.54, 60.25) * mm});
            skLineSegment(sketch, "E8.6.117.0", {"start": v(9.73, 60.22) * mm, "end": v(9.54, 60.25) * mm});
            skLineSegment(sketch, "E8.9.117.0", {"start": v(10.19, 57.86) * mm, "end": v(9.73, 60.22) * mm});
            skLineSegment(sketch, "E8.1.118.0", {"start": v(5.14, 58.53) * mm, "end": v(6.19, 60.69) * mm});
            skLineSegment(sketch, "E8.3.118.0", {"start": v(6.19, 60.69) * mm, "end": v(6.38, 60.67) * mm});
            skLineSegment(sketch, "E8.6.118.0", {"start": v(6.56, 60.65) * mm, "end": v(6.38, 60.67) * mm});
            skLineSegment(sketch, "E8.9.118.0", {"start": v(7.14, 58.31) * mm, "end": v(6.56, 60.65) * mm});
            skLineSegment(sketch, "E8.1.119.0", {"start": v(2.07, 58.71) * mm, "end": v(3, 60.93) * mm});
            skLineSegment(sketch, "E8.3.119.0", {"start": v(3, 60.93) * mm, "end": v(3.2, 60.92) * mm});
            skLineSegment(sketch, "E8.6.119.0", {"start": v(3.38, 60.9) * mm, "end": v(3.2, 60.92) * mm});
            skLineSegment(sketch, "E8.9.119.0", {"start": v(4.08, 58.6) * mm, "end": v(3.38, 60.9) * mm});
            skLineSegment(sketch, "E9.bottom", {"start": v(-35, 35) * mm, "end": v(35, 35) * mm, "construction": true});
            skLineSegment(sketch, "E9.top", {"start": v(-35, -35) * mm, "end": v(35, -35) * mm, "construction": true});
            skLineSegment(sketch, "E9.left", {"start": v(-35, 35) * mm, "end": v(-35, -35) * mm, "construction": true});
            skLineSegment(sketch, "E9.right", {"start": v(35, 35) * mm, "end": v(35, -35) * mm, "construction": true});
            skCircle(sketch, "E10", {"center": v(35, 35) * mm, "radius": 4.1 * mm});
            skCircle(sketch, "E11", {"center": v(-35, 35) * mm, "radius": 4.1 * mm});
            skCircle(sketch, "E12", {"center": v(35, -35) * mm, "radius": 4.1 * mm});
            skCircle(sketch, "E13", {"center": v(-34.67, -34.97) * mm, "radius": 4.1 * mm});
            skCircle(sketch, "E14", {"center": v(0, 0) * mm, "radius": 10 * mm});
            skSolve(sketch);
        }
        {
            var Q0;
            Q0=qSketchRegion(id+"F0",true);
            extrude(context, id + "F1", {"entities" : qUnion([Q0]), "depth" : 10 * mm});
        }
    });
